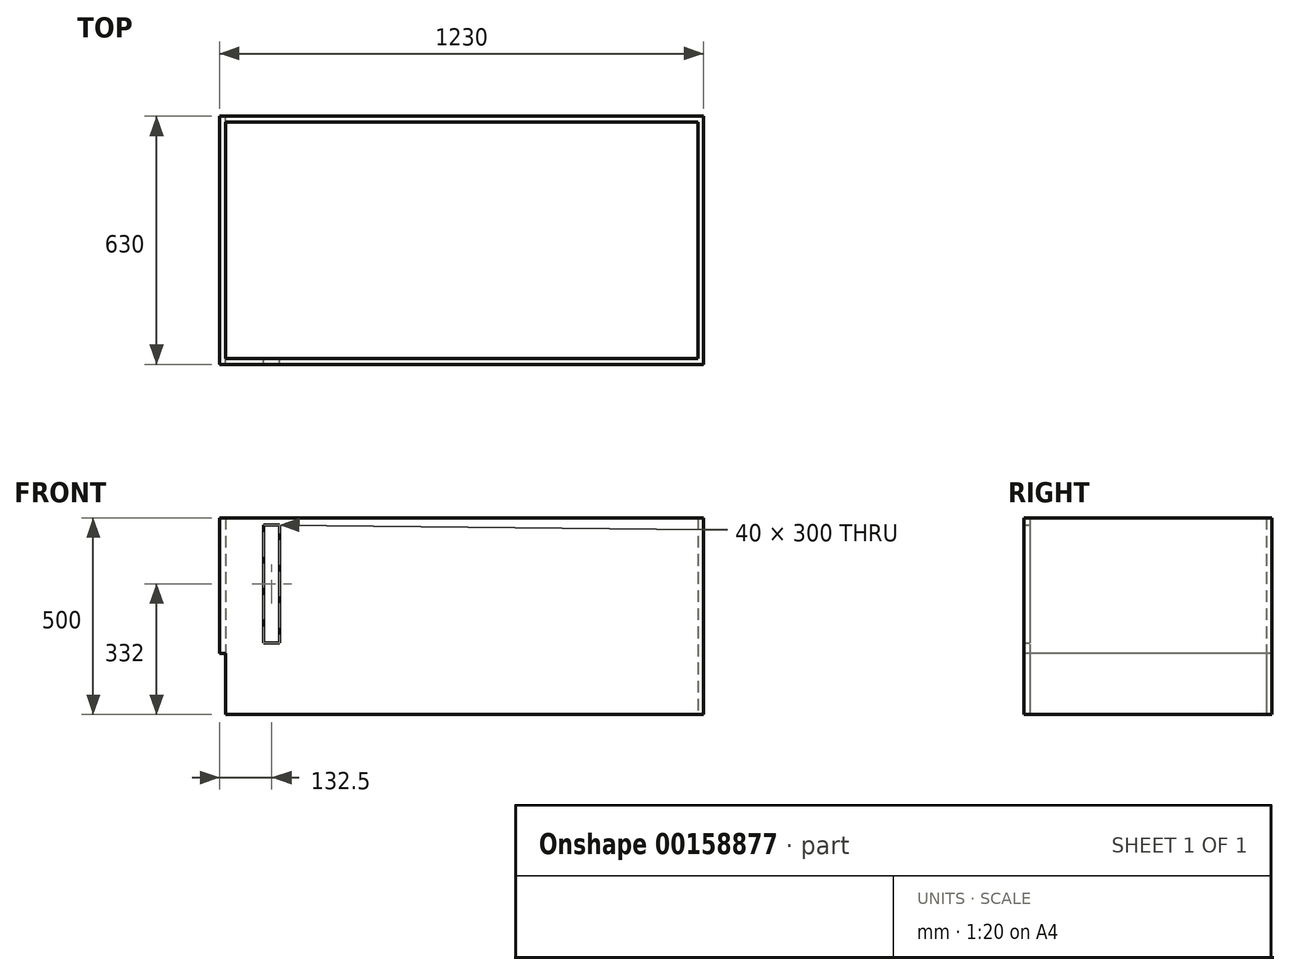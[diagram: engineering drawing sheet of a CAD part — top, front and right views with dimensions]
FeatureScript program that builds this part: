
annotation { "Feature Type Name" : "Feature", "Feature Type Description" : "" }
export const myFeature = defineFeature(function(context is Context, id is Id, definition is map)
    precondition{}
    {
        {
            var Q0;
            Q0=qCreatedBy(makeId("Top.planeOp"),FACE);
            var sketch = newSketch(context, id + "F0", { "sketchPlane" : qUnion([Q0])});
            skLineSegment(sketch, "E0.bottom", {"start": v(-600, -300) * mm, "end": v(600, -300) * mm});
            skLineSegment(sketch, "E0.top", {"start": v(-600, 300) * mm, "end": v(600, 300) * mm});
            skLineSegment(sketch, "E0.left", {"start": v(-600, -300) * mm, "end": v(-600, 300) * mm});
            skLineSegment(sketch, "E0.right", {"start": v(600, -300) * mm, "end": v(600, 300) * mm});
            skPoint(sketch, "E0.middle", {"position": v(0, 0) * mm});
            skLineSegment(sketch, "E1.bottom", {"start": v(-615, -315) * mm, "end": v(615, -315) * mm});
            skLineSegment(sketch, "E1.top", {"start": v(-615, 315) * mm, "end": v(615, 315) * mm});
            skLineSegment(sketch, "E1.left", {"start": v(-615, -315) * mm, "end": v(-615, 315) * mm});
            skLineSegment(sketch, "E1.right", {"start": v(615, -315) * mm, "end": v(615, 315) * mm});
            skSolve(sketch);
        }
        {
            var Q0;
            Q0 = qSketchRegion(id + "F0", true);
            extrude(context, id + "F1", {"entities" : qUnion([Q0]), "depth" : 500 * mm});
        }
        {
            var Q0;
            Q0=makeQuery(id+"F1.opExtrude","SWEPT_FACE",FACE,{"disambiguationData":[OSD([sQuery(id+"F0.wireOp",EDGE,"E0.bottom")])]});
            var sketch = newSketch(context, id + "F2", { "sketchPlane" : qUnion([Q0])});
            skLineSegment(sketch, "E2.bottom", {"start": v(502.5, 482) * mm, "end": v(462.5, 482) * mm});
            skLineSegment(sketch, "E2.top", {"start": v(502.5, 182) * mm, "end": v(462.5, 182) * mm});
            skLineSegment(sketch, "E2.left", {"start": v(502.5, 482) * mm, "end": v(502.5, 182) * mm});
            skLineSegment(sketch, "E2.right", {"start": v(462.5, 482) * mm, "end": v(462.5, 182) * mm});
            skSolve(sketch);
        }
        {
            var Q0;
            Q0=makeQuery(id+"F2.imprint","IMPRINT",FACE,{"disambiguationData":[TD([[makeQuery(id+"F2.imprint","IMPRINT",EDGE,{"derivedFrom":sQuery(id+"F2.wireOp",EDGE,"E2.bottom")}),1.0]])]});
            extrude(context, id + "F3", {"entities" : qUnion([Q0]), "operationType" : NewBodyOperationType.REMOVE, "oppositeDirection" : true, "depth" : 25 * mm});
        }
        {
            var Q0;
            Q0=makeQuery(id+"F1.opExtrude","SWEPT_FACE",FACE,{"disambiguationData":[OSD([sQuery(id+"F0.wireOp",EDGE,"E1.left")])]});
            var sketch = newSketch(context, id + "F4", { "sketchPlane" : qUnion([Q0])});
            skLineSegment(sketch, "E3.bottom", {"start": v(-315, 0) * mm, "end": v(315, 0) * mm});
            skLineSegment(sketch, "E3.top", {"start": v(-315, 155) * mm, "end": v(315, 155) * mm});
            skLineSegment(sketch, "E3.left", {"start": v(-315, 0) * mm, "end": v(-315, 155) * mm});
            skLineSegment(sketch, "E3.right", {"start": v(315, 0) * mm, "end": v(315, 155) * mm});
            skSolve(sketch);
        }
        {
            var Q0;
            Q0 = qSketchRegion(id + "F4", true);
            extrude(context, id + "F5", {"entities" : qUnion([Q0]), "operationType" : NewBodyOperationType.REMOVE, "oppositeDirection" : true, "depth" : 15 * mm});
        }
    });
